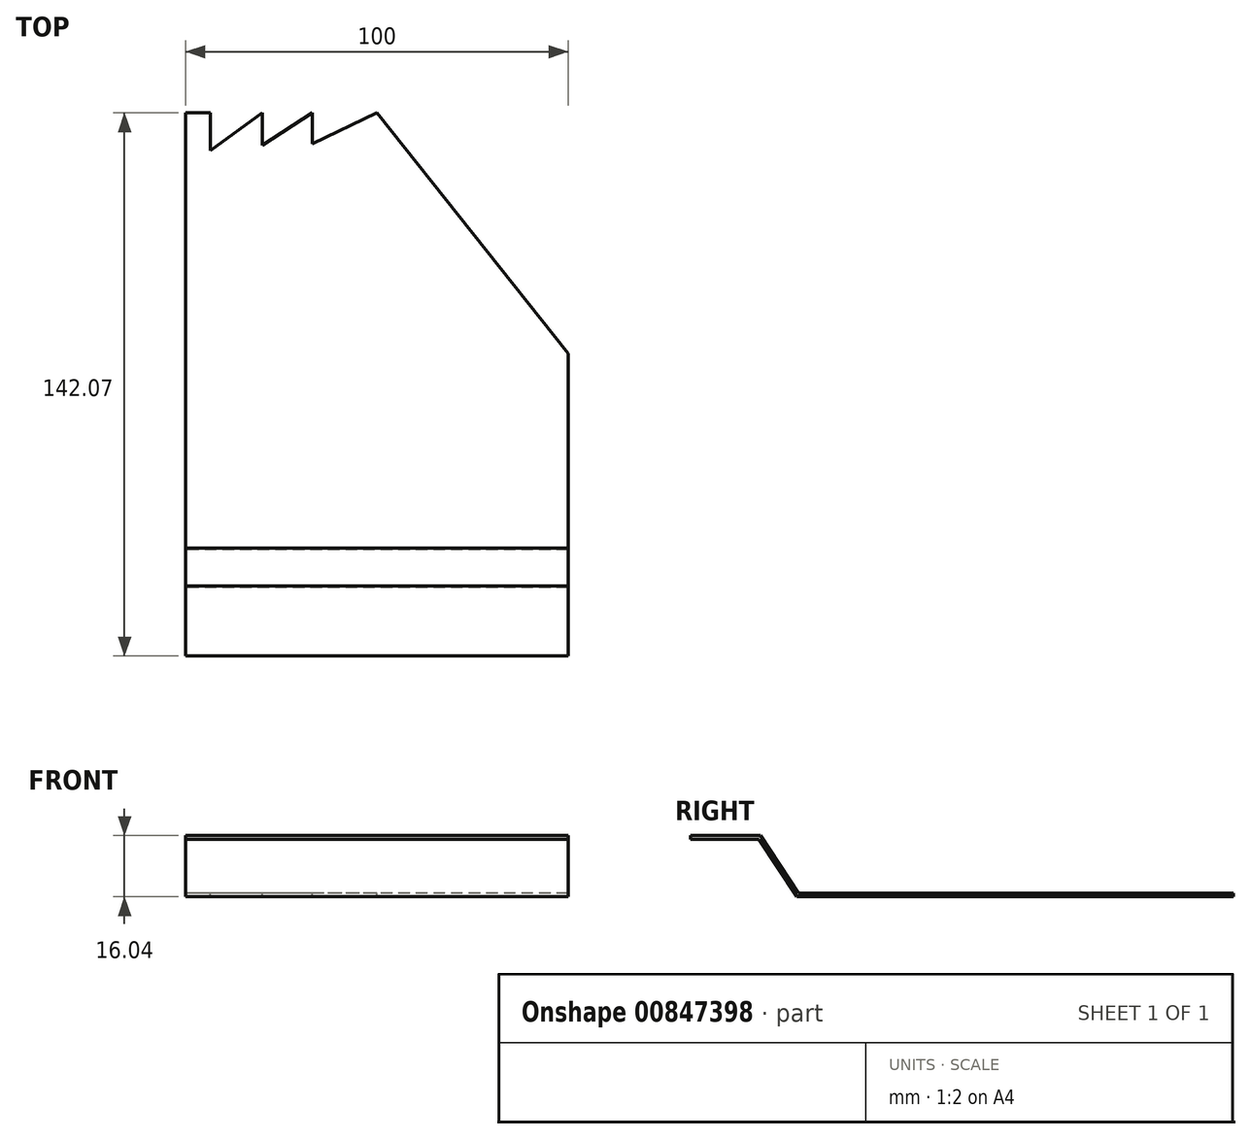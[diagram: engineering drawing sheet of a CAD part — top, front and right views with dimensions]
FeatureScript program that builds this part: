
annotation { "Feature Type Name" : "Feature", "Feature Type Description" : "" }
export const myFeature = defineFeature(function(context is Context, id is Id, definition is map)
    precondition{}
    {
        {
            var Q0;
            Q0=qCreatedBy(makeId("Right.planeOp"),FACE);
            var sketch = newSketch(context, id + "F0", { "sketchPlane" : qUnion([Q0])});
            skLineSegment(sketch, "E0.bottom", {"start": v(-38.85, 0.5) * mm, "end": v(75, 0.5) * mm});
            skLineSegment(sketch, "E0.top", {"start": v(-39.19, -0.5) * mm, "end": v(75, -0.5) * mm});
            skLineSegment(sketch, "E0.right", {"start": v(75, 0.5) * mm, "end": v(75, -0.5) * mm});
            skPoint(sketch, "E0.middle", {"position": v(0, 0) * mm});
            skLineSegment(sketch, "E1", {"start": v(-39.85, 0.5) * mm, "end": v(-49.1, 14.54) * mm});
            skLineSegment(sketch, "E2", {"start": v(-49.1, 14.54) * mm, "end": v(-67.07, 14.54) * mm});
            skLineSegment(sketch, "E3", {"start": v(-67.07, 14.54) * mm, "end": v(-67.07, 15.54) * mm});
            skLineSegment(sketch, "E4", {"start": v(-38.85, 0.5) * mm, "end": v(-48.76, 15.54) * mm});
            skLineSegment(sketch, "E5", {"start": v(-67.07, 15.54) * mm, "end": v(-48.76, 15.54) * mm});
            skLineSegment(sketch, "E6", {"start": v(-39.85, 0.5) * mm, "end": v(-39.19, -0.5) * mm});
            skPoint(sketch, "E0.left.end.orphan", {"position": v(-75, -0.5) * mm});
            skPoint(sketch, "E0.left.start.orphan", {"position": v(-75, 0.5) * mm});
            skSolve(sketch);
        }
        {
            var Q0;
            Q0=qSketchRegion(id+"F0",true);
            extrude(context, id + "F1", {"entities" : qUnion([Q0]), "depth" : 100 * mm, "offsetDistance" : 25 * mm});
        }
        {
            var Q0;
            Q0=makeQuery(id+"F1.opExtrude","SWEPT_FACE",FACE,{"disambiguationData":[OSD([sQuery(id+"F0.wireOp",EDGE,"E0.bottom")])]});
            var sketch = newSketch(context, id + "F2", { "sketchPlane" : qUnion([Q0])});
            skLineSegment(sketch, "E7", {"start": v(100, 12) * mm, "end": v(50, 75) * mm});
            skLineSegment(sketch, "E8", {"start": v(50, 75) * mm, "end": v(33.07, 66.95) * mm});
            skLineSegment(sketch, "E9", {"start": v(33.07, 66.95) * mm, "end": v(33.07, 75) * mm});
            skLineSegment(sketch, "E10", {"start": v(33.07, 75) * mm, "end": v(19.98, 66.48) * mm});
            skLineSegment(sketch, "E11", {"start": v(19.98, 66.48) * mm, "end": v(19.98, 75) * mm});
            skLineSegment(sketch, "E12", {"start": v(19.98, 75) * mm, "end": v(6.37, 65.1) * mm});
            skLineSegment(sketch, "E13", {"start": v(6.37, 65.1) * mm, "end": v(6.37, 75) * mm});
            skLineSegment(sketch, "E14", {"start": v(6.37, 75) * mm, "end": v(16.86, 99.32) * mm});
            skLineSegment(sketch, "E15", {"start": v(16.86, 99.32) * mm, "end": v(155, 119.25) * mm});
            skLineSegment(sketch, "E16", {"start": v(155, 119.25) * mm, "end": v(100, 12) * mm});
            skSolve(sketch);
        }
        {
            var Q0;
            {var subQ0=sQuery(id+"F2.wireOp",EDGE,"E8");Q0=makeQuery(id+"F2.imprint","IMPRINT",FACE,{"disambiguationData":[TD([[makeQuery(id+"F2.imprint","IMPRINT",EDGE,{"derivedFrom":subQ0}),-1.0]])]});}
            var Q1;
            {var subQ0=sQuery(id+"F2.wireOp",EDGE,"E10");Q1=makeQuery(id+"F2.imprint","IMPRINT",FACE,{"disambiguationData":[TD([[makeQuery(id+"F2.imprint","IMPRINT",EDGE,{"derivedFrom":subQ0}),-1.0]])]});}
            var Q2;
            {var subQ0=sQuery(id+"F2.wireOp",EDGE,"E12");Q2=makeQuery(id+"F2.imprint","IMPRINT",FACE,{"disambiguationData":[TD([[makeQuery(id+"F2.imprint","IMPRINT",EDGE,{"derivedFrom":subQ0}),-1.0]])]});}
            var Q3;
            {var subQ0=sQuery(id+"F2.wireOp",EDGE,"E7");Q3=makeQuery(id+"F2.imprint","IMPRINT",FACE,{"disambiguationData":[TD([[makeQuery(id+"F2.imprint","IMPRINT",EDGE,{"derivedFrom":subQ0}),-1.0]])]});}
            var Q4;
            {var subQ7=sQuery(id+"F2.wireOp",EDGE,"E14");Q4=makeQuery(id+"F2.imprint","IMPRINT",FACE,{"disambiguationData":[TD([[makeQuery(id+"F2.imprint","IMPRINT",EDGE,{"derivedFrom":subQ7}),-1.0]])]});}
            extrude(context, id + "F3", {"entities" : qUnion([Q0, Q1, Q2, Q3, Q4]), "operationType" : NewBodyOperationType.REMOVE, "oppositeDirection" : true, "depth" : 25 * mm, "offsetDistance" : 25 * mm});
        }
    });
